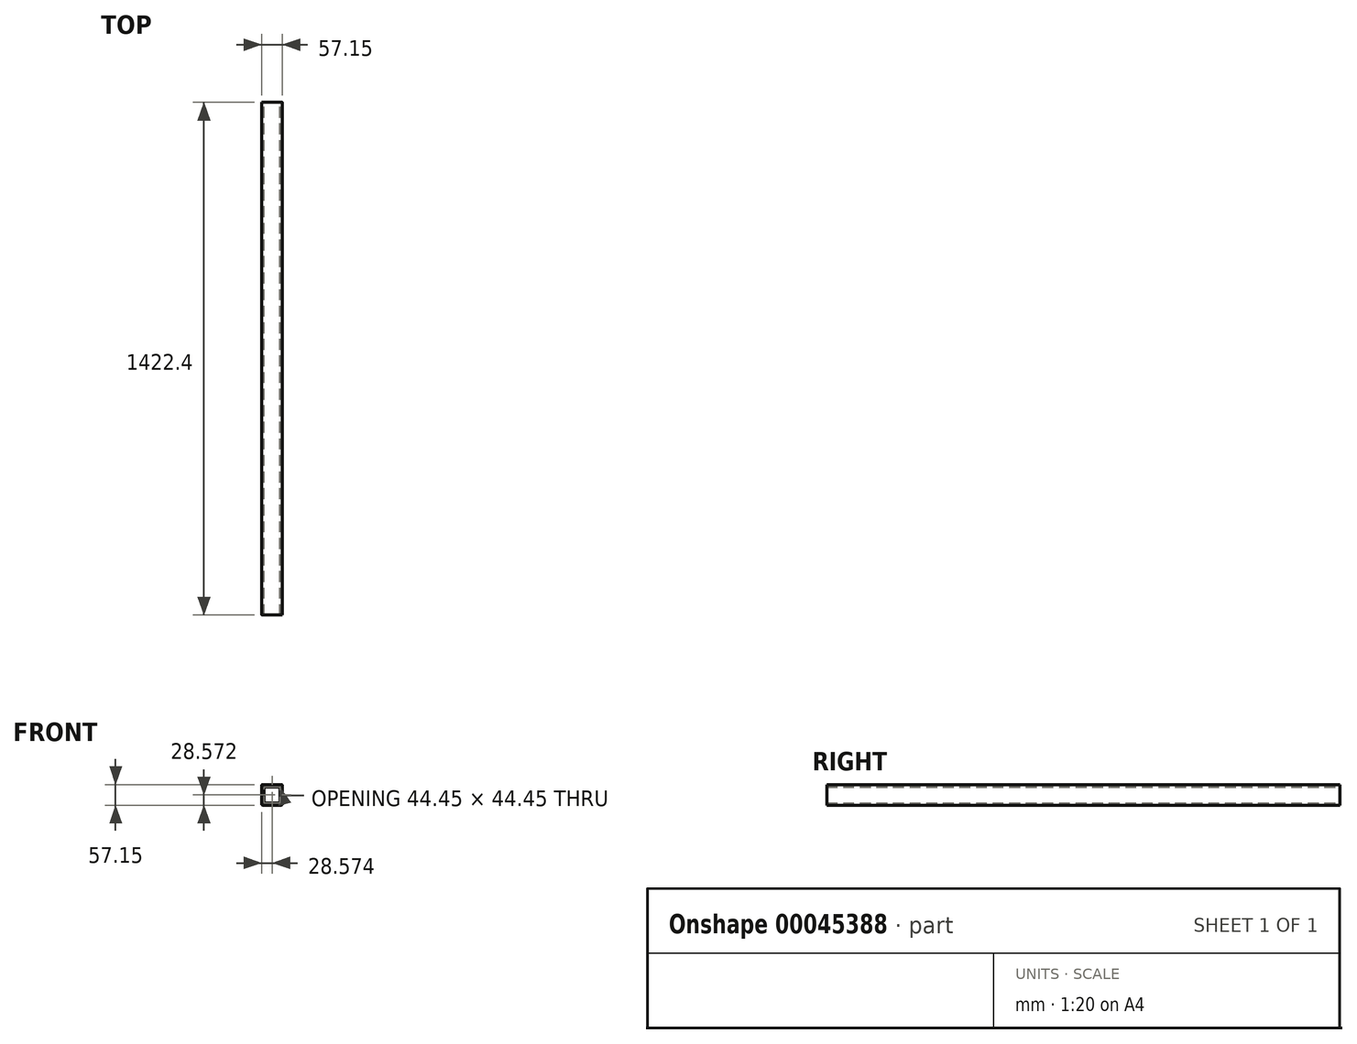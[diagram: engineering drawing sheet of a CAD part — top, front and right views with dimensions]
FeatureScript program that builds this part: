
annotation { "Feature Type Name" : "Feature", "Feature Type Description" : "" }
export const myFeature = defineFeature(function(context is Context, id is Id, definition is map)
    precondition{}
    {
        {
            var Q0;
            Q0=qCreatedBy(makeId("Front.planeOp"),FACE);
            var sketch = newSketch(context, id + "F0", { "sketchPlane" : qUnion([Q0])});
            skLineSegment(sketch, "E0.bottom", {"start": v(-27.58, 35.03) * mm, "end": v(24.49, 35.03) * mm});
            skLineSegment(sketch, "E0.top", {"start": v(-27.58, -22.12) * mm, "end": v(24.49, -22.12) * mm});
            skLineSegment(sketch, "E0.left", {"start": v(-30.12, 32.49) * mm, "end": v(-30.12, -19.58) * mm});
            skLineSegment(sketch, "E0.right", {"start": v(27.03, 32.49) * mm, "end": v(27.03, -19.58) * mm});
            skLineSegment(sketch, "E1.bottom", {"start": v(-21.23, 28.68) * mm, "end": v(20.68, 28.68) * mm});
            skLineSegment(sketch, "E1.top", {"start": v(-21.23, -15.77) * mm, "end": v(18.14, -15.77) * mm});
            skLineSegment(sketch, "E1.left", {"start": v(-23.77, 26.14) * mm, "end": v(-23.77, -13.23) * mm});
            skLineSegment(sketch, "E1.right", {"start": v(20.68, 28.68) * mm, "end": v(20.68, -13.23) * mm});
            skPoint(sketch, "E2.visualSharp", {"position": v(-30.12, 35.03) * mm});
            skArc(sketch, "E2.filletArc", {"start": v(-27.58, 35.03) * mm, "mid": v(-29.38, 34.28) * mm, "end": v(-30.12, 32.49) * mm});
            skPoint(sketch, "E3.visualSharp", {"position": v(-23.77, 28.68) * mm});
            skArc(sketch, "E3.filletArc", {"start": v(-21.23, 28.68) * mm, "mid": v(-23.03, 27.93) * mm, "end": v(-23.77, 26.14) * mm});
            skPoint(sketch, "E4.visualSharp", {"position": v(-30.12, -22.12) * mm});
            skArc(sketch, "E4.filletArc", {"start": v(-30.12, -19.58) * mm, "mid": v(-29.38, -21.38) * mm, "end": v(-27.58, -22.12) * mm});
            skPoint(sketch, "E5.visualSharp", {"position": v(-23.77, -15.77) * mm});
            skArc(sketch, "E5.filletArc", {"start": v(-23.77, -13.23) * mm, "mid": v(-23.03, -15.03) * mm, "end": v(-21.23, -15.77) * mm});
            skPoint(sketch, "E6.visualSharp", {"position": v(20.68, -15.77) * mm});
            skArc(sketch, "E6.filletArc", {"start": v(18.14, -15.77) * mm, "mid": v(19.93, -15.03) * mm, "end": v(20.68, -13.23) * mm});
            skPoint(sketch, "E7.visualSharp", {"position": v(27.03, -22.12) * mm});
            skArc(sketch, "E7.filletArc", {"start": v(24.49, -22.12) * mm, "mid": v(26.28, -21.38) * mm, "end": v(27.03, -19.58) * mm});
            skPoint(sketch, "E8.visualSharp", {"position": v(27.03, 35.03) * mm});
            skArc(sketch, "E8.filletArc", {"start": v(27.03, 32.49) * mm, "mid": v(26.28, 34.28) * mm, "end": v(24.49, 35.03) * mm});
            skSolve(sketch);
        }
        {
            var Q0;
            Q0=makeQuery(id+"F0.imprint","IMPRINT",FACE,{"disambiguationData":[TD([[makeQuery(id+"F0.imprint","IMPRINT",EDGE,{"derivedFrom":sQuery(id+"F0.wireOp",EDGE,"E0.bottom")}),-1.0]])]});
            extrude(context, id + "F1", {"entities" : qUnion([Q0]), "depth" : 1422.4 * mm});
        }
    });
